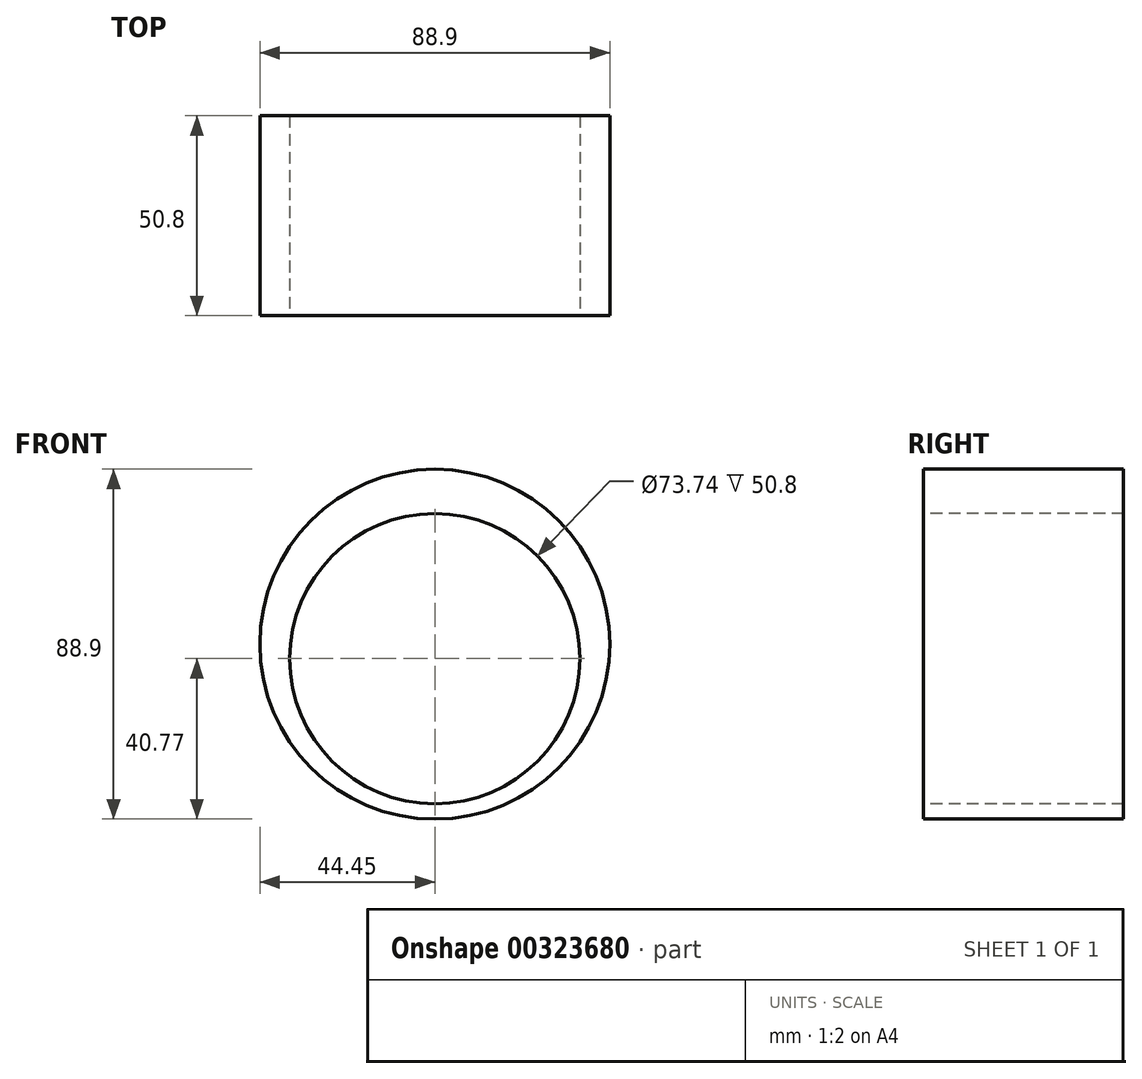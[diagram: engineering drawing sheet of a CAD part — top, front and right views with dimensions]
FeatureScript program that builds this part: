
annotation { "Feature Type Name" : "Feature", "Feature Type Description" : "" }
export const myFeature = defineFeature(function(context is Context, id is Id, definition is map)
    precondition{}
    {
        {
            var Q0;
            Q0=qCreatedBy(makeId("Front.planeOp"),FACE);
            var sketch = newSketch(context, id + "F0", { "sketchPlane" : qUnion([Q0])});
            skCircle(sketch, "E0", {"center": v(0, 3.68) * mm, "radius": 44.45 * mm});
            skSolve(sketch);
        }
        {
            var Q0;
            Q0 = qSketchRegion(id + "F0", true);
            extrude(context, id + "F1", {"entities" : qUnion([Q0]), "depth" : 50.8 * mm});
        }
        {
            var Q0;
            Q0=makeQuery(id+"F1.opExtrude","CAP_FACE",FACE,{"disambiguationData":[OSD([sQuery(id+"F0.wireOp",EDGE,"E0")])],"isStart":false});
            var sketch = newSketch(context, id + "F2", { "sketchPlane" : qUnion([Q0])});
            skCircle(sketch, "E1", {"center": v(0, 0) * mm, "radius": 36.87 * mm});
            skSolve(sketch);
        }
        {
            var Q0;
            Q0 = qSketchRegion(id + "F2", true);
            var Q1;
            Q1=makeQuery(id+"F1.opExtrude","CAP_FACE",FACE,{"disambiguationData":[OSD([sQuery(id+"F0.wireOp",EDGE,"E0")])],"isStart":true});
            extrude(context, id + "F3", {"entities" : qUnion([Q0, Q1]), "operationType" : NewBodyOperationType.REMOVE, "oppositeDirection" : true, "depth" : 76.2 * mm});
        }
    });
